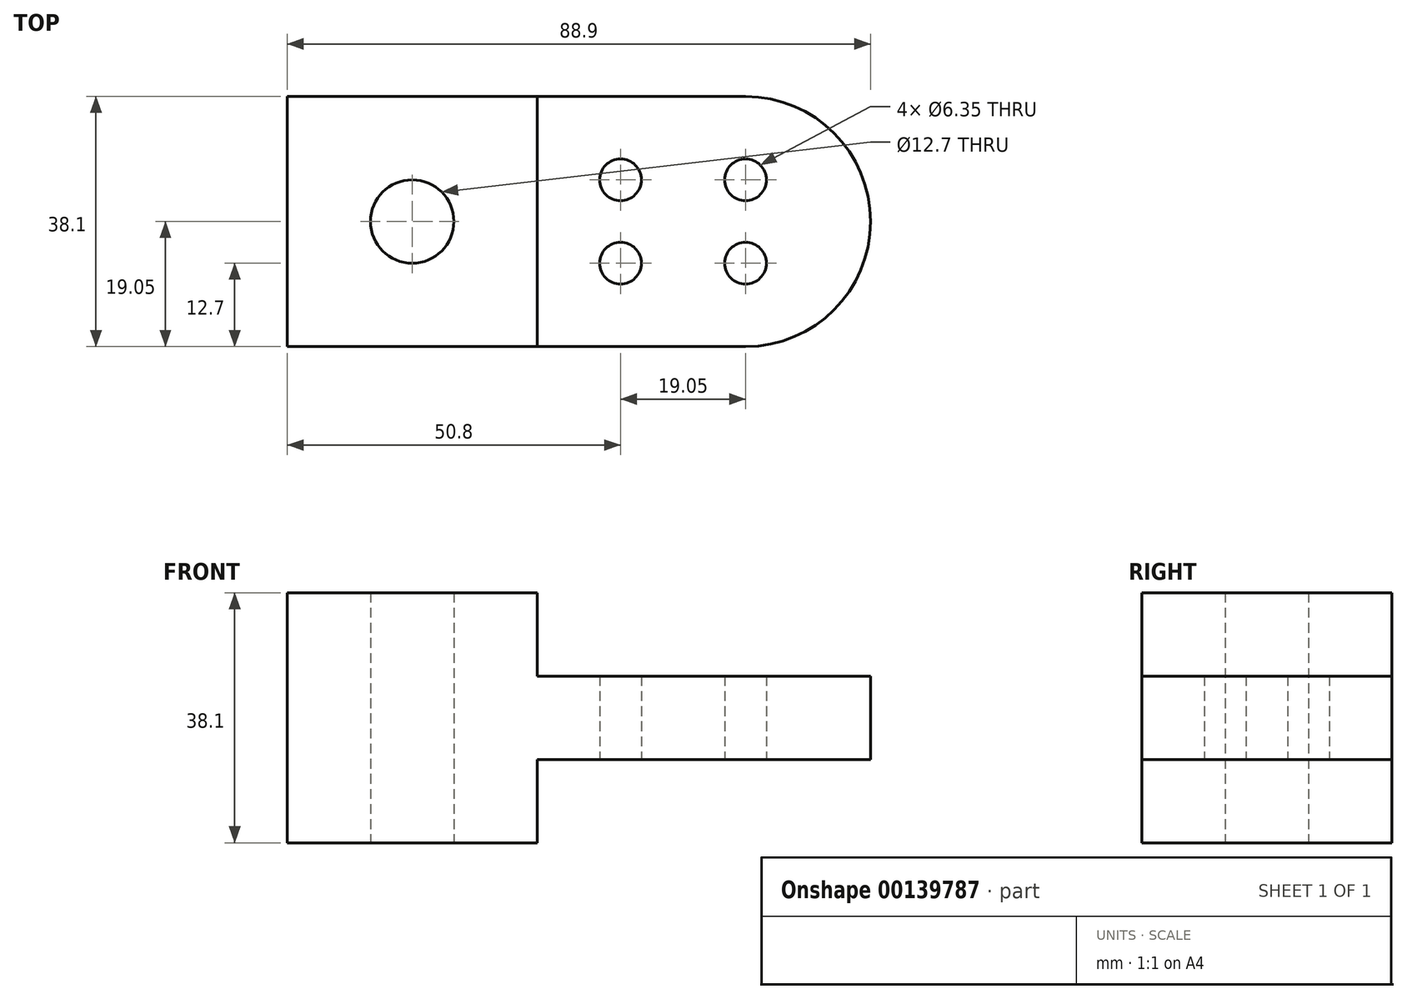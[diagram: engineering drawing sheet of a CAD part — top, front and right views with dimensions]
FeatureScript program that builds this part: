
annotation { "Feature Type Name" : "Feature", "Feature Type Description" : "" }
export const myFeature = defineFeature(function(context is Context, id is Id, definition is map)
    precondition{}
    {
        {
            var Q0;
            Q0=qCreatedBy(makeId("Top.planeOp"),FACE);
            var sketch = newSketch(context, id + "F0", { "sketchPlane" : qUnion([Q0])});
            skCircle(sketch, "E0", {"center": v(0, 0) * mm, "radius": 6.35 * mm});
            skLineSegment(sketch, "E1.bottom", {"start": v(-19.05, 19.05) * mm, "end": v(19.05, 19.05) * mm});
            skLineSegment(sketch, "E1.top", {"start": v(-19.05, -19.05) * mm, "end": v(19.05, -19.05) * mm});
            skLineSegment(sketch, "E1.left", {"start": v(-19.05, 19.05) * mm, "end": v(-19.05, -19.05) * mm});
            skLineSegment(sketch, "E1.right", {"start": v(19.05, 19.05) * mm, "end": v(19.05, -19.05) * mm});
            skLineSegment(sketch, "E2.bottom", {"start": v(19.05, 19.05) * mm, "end": v(50.8, 19.05) * mm});
            skLineSegment(sketch, "E2.top", {"start": v(19.05, -19.05) * mm, "end": v(50.8, -19.05) * mm});
            skArc(sketch, "E3", {"start": v(50.8, -19.05) * mm, "mid": v(69.85, 0) * mm, "end": v(50.8, 19.05) * mm});
            skCircle(sketch, "E4", {"center": v(50.8, 6.35) * mm, "radius": 3.18 * mm});
            skCircle(sketch, "E5", {"center": v(50.8, -6.35) * mm, "radius": 3.18 * mm});
            skCircle(sketch, "E6", {"center": v(31.75, -6.35) * mm, "radius": 3.18 * mm});
            skCircle(sketch, "E7", {"center": v(31.75, 6.35) * mm, "radius": 3.18 * mm});
            skSolve(sketch);
        }
        {
            var Q0;
            Q0=makeQuery(id+"F0.imprint","IMPRINT",FACE,{"disambiguationData":[TD([[makeQuery(id+"F0.imprint","IMPRINT",EDGE,{"derivedFrom":sQuery(id+"F0.wireOp",EDGE,"E0")}),-1.0]])]});
            extrude(context, id + "F1", {"entities" : qUnion([Q0]), "endBound" : BoundingType.SYMMETRIC, "depth" : 38.1 * mm});
        }
        {
            var Q0;
            Q0=makeQuery(id+"F0.imprint","IMPRINT",FACE,{"disambiguationData":[TD([[makeQuery(id+"F0.imprint","IMPRINT",EDGE,{"derivedFrom":sQuery(id+"F0.wireOp",EDGE,"E2.bottom")}),-1.0]])]});
            extrude(context, id + "F2", {"entities" : qUnion([Q0]), "operationType" : NewBodyOperationType.ADD, "endBound" : BoundingType.SYMMETRIC, "depth" : 12.7 * mm});
        }
    });
